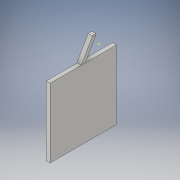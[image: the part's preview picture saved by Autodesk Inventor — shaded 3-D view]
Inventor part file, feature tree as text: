
AUTODESK INVENTOR PART (.ipt)
format: ipt  version: 2017 (Build 210142000, 142)  size: 152,576 bytes
history: native  units: in
note: dims shown in document units (in); Inventor stores cm internally (conversion verified against a paired STEP export)
features: sketch x9, extrude x7, projected_geometry x1
ambient origin geometry x8: Origin, YZ Plane, XZ Plane, XY Plane, X Axis, Y Axis, Z Axis, Center Point
bodies: Solid1 (feature_tree)
feature tree (17):
  extrude  "Extrusion1"  Depth=0.125in
  sketch  "Sketch2"  dims[d2=1.0in d3=0.0in d7=0.125in d8=0.0in]
  extrude  "Extrusion2"  Depth=0.125in TaperAngle=0.0deg
  extrude  "Extrusion3"  Depth=0.125in TaperAngle=0.0deg
  sketch  "Sketch5"  dims[d17=1.0in d18=0.0in]
  extrude  "Extrusion4"  Depth=1.0in TaperAngle=0.0deg
  extrude  "Extrusion5"  [1 undecoded]
  extrude  "Extrusion6"  [1 undecoded]
  extrude  "Extrusion7"  [1 undecoded]
  sketch  "Sketch1"  dims[d0=2.21in d1=0.125in]
  projected_geometry  "Projected Loop1"
  sketch  "Sketch3"  dims[d9=1.0in d10=0.0in d11=0.125in d12=0.0in]
  sketch  "Sketch4"  dims[d13=1.0in d14=0.0in d15=1.0in d16=0.0in]
  sketch  "Sketch6"
  sketch  "Sketch7"
  sketch  "Sketch8"
  sketch  "Sketch9"
note: 3 required parameter values undecoded (feature->parameter linkage not recoverable at this tier; creation-order binding heuristic only, values carry confidence <= 0.55)
